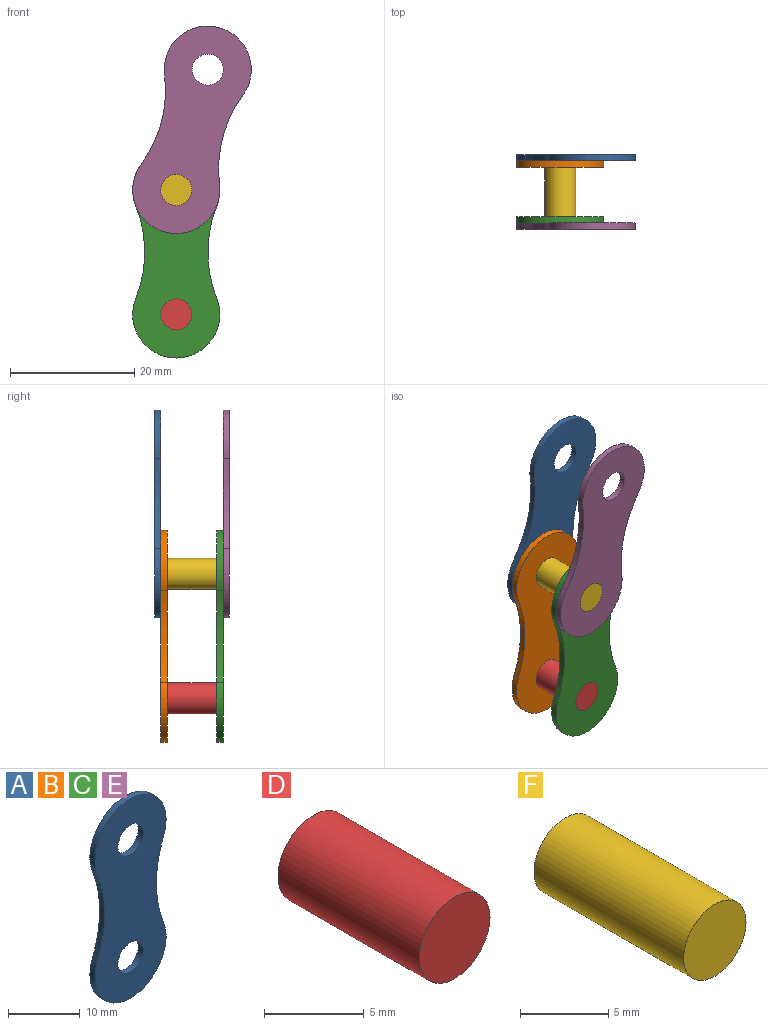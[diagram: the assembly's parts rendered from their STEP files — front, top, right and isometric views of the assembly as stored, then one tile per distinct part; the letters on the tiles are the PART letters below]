
ASSEMBLY  parts=6 mates=6
PART A: 8 faces, bbox 14x1x34 mm
  f0: cylinder r=20mm len=14.82mm, axis (0,1,0), area 15.2mm2, adj f1,f5,f6,f7
  f1: cylinder r=7mm len=14mm, axis (0,1,0), area 27.3mm2, adj f0,f2,f6,f7
  f2: cylinder r=20mm len=14.82mm, axis (0,1,0), area 15.2mm2, adj f1,f5,f6,f7
  f3: cylinder r=2.5mm len=5mm, axis (0,1,0), area 15.7mm2, adj f6,f7
  f4: cylinder r=2.5mm len=5mm, axis (0,1,0), area 15.7mm2, adj f6,f7
  f5: cylinder r=7mm len=14mm, axis (0,1,0), area 27.3mm2, adj f0,f2,f6,f7
  f6: plane 34x14mm, normal (0,-1,0), area 349.9mm2, adj f0,f1,f2,f3,f4,f5
  f7: plane 34x14mm, normal (0,1,0), area 349.9mm2, adj f0,f1,f2,f3,f4,f5
PART B: same geometry as A
PART C: same geometry as A
PART D: 3 faces, bbox 5x10x5 mm
  f0: cylinder r=2.5mm len=10mm, axis (0,1,0), area 157.1mm2, adj f1,f2
  f1: plane 5x5mm, normal (0,-1,0), area 19.6mm2, adj f0
  f2: plane 5x5mm, normal (0,1,0), area 19.6mm2, adj f0
PART E: same geometry as A
PART F: 3 faces, bbox 5x12x5 mm
  f0: cylinder r=2.5mm len=12mm, axis (0,1,0), area 188.5mm2, adj f1,f2
  f1: plane 5x5mm, normal (0,-1,0), area 19.6mm2, adj f0
  f2: plane 5x5mm, normal (0,1,0), area 19.6mm2, adj f0
PLACE A rot(axis=(0,1,0),14.6deg) t=(3.45,6.93,18.05)mm
PLACE B t=(-1.61,5.93,-1.31)mm fixed
PLACE C t=(-1.61,-3.07,-1.31)mm
PLACE D t=(-1.61,5.93,-21.31)mm
PLACE E rot(axis=(0,1,0),14.6deg) t=(3.45,-4.07,18.05)mm
PLACE F rot(axis=(0,1,0),14.6deg) t=(-1.61,6.93,-1.31)mm
MATE revolute B.f3 <-> A.f1  axis (0,1,0) through (-1.61,5.93,-1.31)mm
MATE fastened D.f0 <-> C.f1  axis (0,-1,0) through (-1.61,-4.07,-21.31)mm
MATE fastened D.f0 <-> B.f1  axis (0,1,0) through (-1.61,5.93,-21.31)mm
MATE revolute C.f3 <-> E.f1  axis (0,-1,0) through (-1.61,-4.07,-1.31)mm
MATE fastened F.f0 <-> A.f1  axis (0,1,0) through (-1.61,6.93,-1.31)mm
MATE fastened F.f0 <-> E.f1  axis (0,-1,0) through (-1.61,-5.07,-1.31)mm
